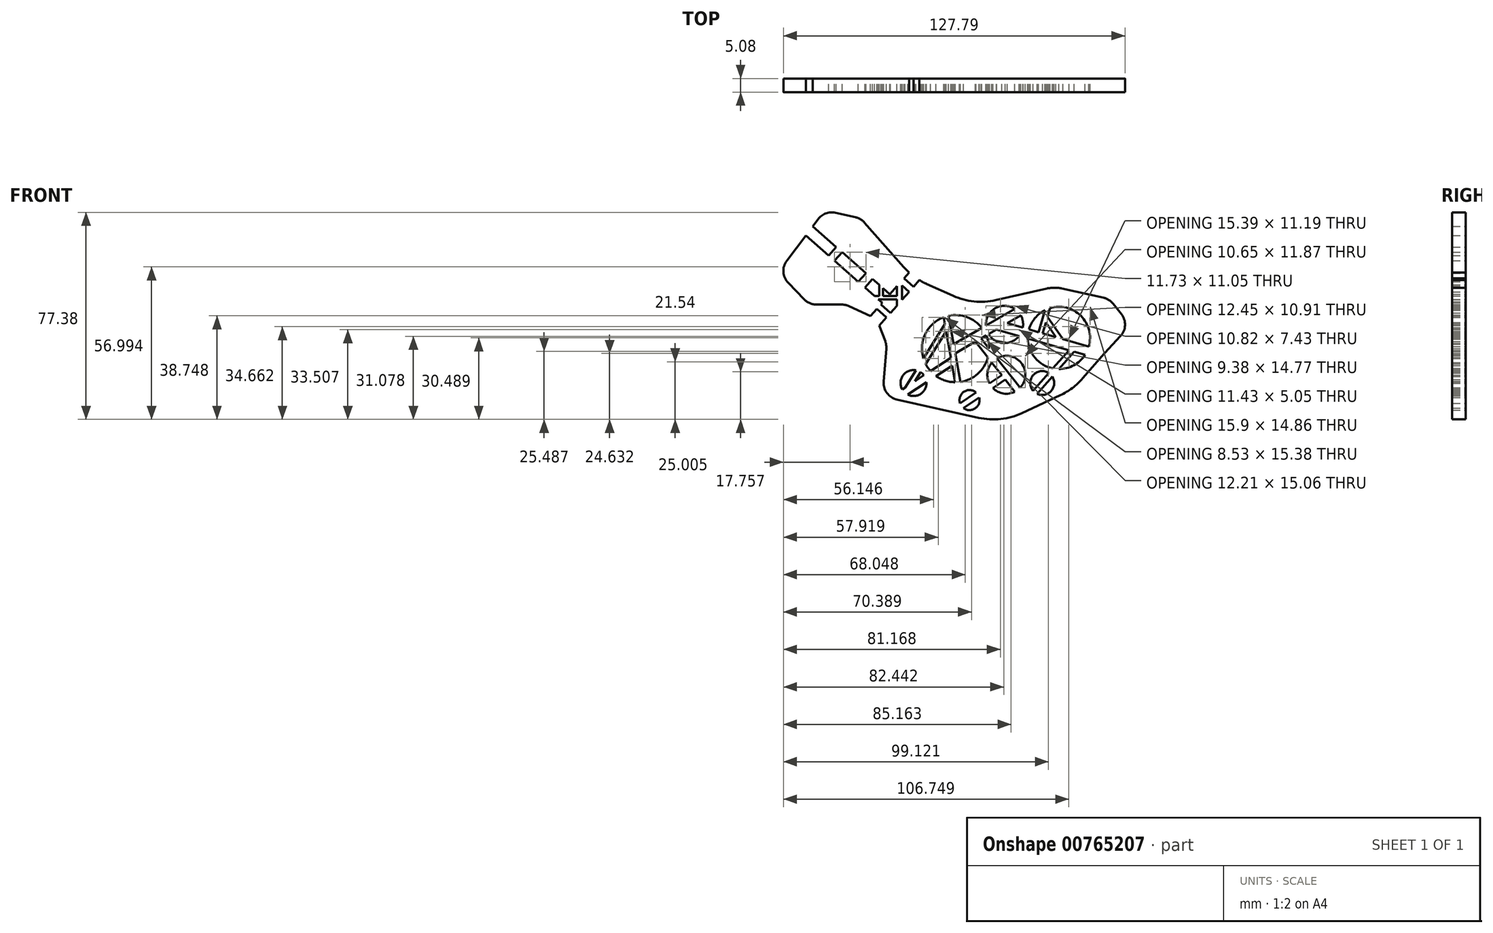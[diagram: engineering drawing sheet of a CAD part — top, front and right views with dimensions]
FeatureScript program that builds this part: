
annotation { "Feature Type Name" : "Feature", "Feature Type Description" : "" }
export const myFeature = defineFeature(function(context is Context, id is Id, definition is map)
    precondition{}
    {
        {
            var Q0;
            Q0=qCreatedBy(makeId("Front.planeOp"),FACE);
            var sketch = newSketch(context, id + "F0", { "sketchPlane" : qUnion([Q0])});
            skLineSegment(sketch, "E0", {"start": v(-47.4, 34.58) * mm, "end": v(-40.28, 44.05) * mm});
            skLineSegment(sketch, "E1", {"start": v(-29.25, 52.5) * mm, "end": v(-21.71, 50.83) * mm});
            skLineSegment(sketch, "E2", {"start": v(-18.34, 48.84) * mm, "end": v(-3.61, 32.2) * mm});
            skLineSegment(sketch, "E3", {"start": v(4.97, 25.88) * mm, "end": v(14.76, 21.48) * mm});
            skLineSegment(sketch, "E4", {"start": v(30.8, 19.86) * mm, "end": v(49.9, 24.2) * mm});
            skLineSegment(sketch, "E5", {"start": v(55.46, 24.2) * mm, "end": v(71.08, 20.73) * mm});
            skLineSegment(sketch, "E6", {"start": v(74.67, 18.5) * mm, "end": v(77.72, 14.67) * mm});
            skLineSegment(sketch, "E7", {"start": v(77.4, 6.37) * mm, "end": v(71.52, 0.08) * mm});
            skLineSegment(sketch, "E8", {"start": v(71.36, -0.09) * mm, "end": v(63.3, -9.36) * mm});
            skLineSegment(sketch, "E9", {"start": v(54.85, -15.72) * mm, "end": v(40.59, -22.36) * mm});
            skLineSegment(sketch, "E10", {"start": v(24.36, -24.13) * mm, "end": v(3.63, -19.52) * mm});
            skLineSegment(sketch, "E11", {"start": v(3.63, -19.52) * mm, "end": v(-6.19, -17.34) * mm});
            skLineSegment(sketch, "E12", {"start": v(-11.14, -10.65) * mm, "end": v(-10.18, 1.76) * mm});
            skLineSegment(sketch, "E13", {"start": v(-10.57, 4.47) * mm, "end": v(-12.77, 10.34) * mm});
            skLineSegment(sketch, "E14", {"start": v(-16.05, 13.88) * mm, "end": v(-24.15, 17.61) * mm});
            skLineSegment(sketch, "E15", {"start": v(-26.81, 18.2) * mm, "end": v(-36.27, 18.2) * mm});
            skLineSegment(sketch, "E16", {"start": v(-40.82, 20.11) * mm, "end": v(-46.88, 26.33) * mm});
            skPoint(sketch, "E17.visualSharp", {"position": v(-33.24, 53.4) * mm});
            skArc(sketch, "E17.filletArc", {"start": v(-29.25, 52.5) * mm, "mid": v(-32.82, 52.26) * mm, "end": v(-35.7, 50.13) * mm});
            skPoint(sketch, "E18.visualSharp", {"position": v(-19.7, 50.38) * mm});
            skArc(sketch, "E18.filletArc", {"start": v(-18.34, 48.84) * mm, "mid": v(-19.87, 50.1) * mm, "end": v(-21.71, 50.83) * mm});
            skPoint(sketch, "E19.visualSharp", {"position": v(0, 28.12) * mm});
            skArc(sketch, "E19.filletArc", {"start": v(-3.61, 32.2) * mm, "mid": v(-2.66, 31.19) * mm, "end": v(-1.65, 30.22) * mm});
            skPoint(sketch, "E20.visualSharp", {"position": v(22.5, 17.98) * mm});
            skArc(sketch, "E20.filletArc", {"start": v(14.76, 21.48) * mm, "mid": v(22.65, 19.36) * mm, "end": v(30.8, 19.86) * mm});
            skPoint(sketch, "E21.visualSharp", {"position": v(52.68, 24.82) * mm});
            skArc(sketch, "E21.filletArc", {"start": v(55.46, 24.2) * mm, "mid": v(52.68, 24.5) * mm, "end": v(49.9, 24.2) * mm});
            skPoint(sketch, "E22.visualSharp", {"position": v(73.27, 20.25) * mm});
            skArc(sketch, "E22.filletArc", {"start": v(74.67, 18.5) * mm, "mid": v(73.07, 19.92) * mm, "end": v(71.08, 20.73) * mm});
            skPoint(sketch, "E23.visualSharp", {"position": v(81.14, 10.38) * mm});
            skArc(sketch, "E23.filletArc", {"start": v(77.4, 6.37) * mm, "mid": v(79.1, 10.46) * mm, "end": v(77.72, 14.67) * mm});
            skPoint(sketch, "E24.visualSharp", {"position": v(71.44, 0) * mm});
            skArc(sketch, "E24.filletArc", {"start": v(71.52, 0.08) * mm, "mid": v(71.44, 0) * mm, "end": v(71.36, -0.09) * mm});
            skPoint(sketch, "E25.visualSharp", {"position": v(59.75, -13.44) * mm});
            skArc(sketch, "E25.filletArc", {"start": v(54.85, -15.72) * mm, "mid": v(59.41, -12.98) * mm, "end": v(63.3, -9.36) * mm});
            skPoint(sketch, "E26.visualSharp", {"position": v(32.77, -26) * mm});
            skArc(sketch, "E26.filletArc", {"start": v(24.36, -24.13) * mm, "mid": v(32.62, -24.58) * mm, "end": v(40.59, -22.36) * mm});
            skPoint(sketch, "E27.visualSharp", {"position": v(-11.57, -16.14) * mm});
            skArc(sketch, "E27.filletArc", {"start": v(-11.14, -10.65) * mm, "mid": v(-9.91, -14.92) * mm, "end": v(-6.19, -17.34) * mm});
            skPoint(sketch, "E28.visualSharp", {"position": v(-10.08, 3.16) * mm});
            skArc(sketch, "E28.filletArc", {"start": v(-10.18, 1.76) * mm, "mid": v(-10.23, 3.14) * mm, "end": v(-10.57, 4.47) * mm});
            skPoint(sketch, "E29.visualSharp", {"position": v(-13.69, 12.78) * mm});
            skPoint(sketch, "E30.visualSharp", {"position": v(-25.42, 18.2) * mm});
            skArc(sketch, "E30.filletArc", {"start": v(-24.15, 17.61) * mm, "mid": v(-25.45, 18.05) * mm, "end": v(-26.81, 18.2) * mm});
            skPoint(sketch, "E31.visualSharp", {"position": v(-38.95, 18.2) * mm});
            skArc(sketch, "E31.filletArc", {"start": v(-40.82, 20.11) * mm, "mid": v(-38.74, 18.7) * mm, "end": v(-36.27, 18.2) * mm});
            skPoint(sketch, "E32.visualSharp", {"position": v(-50.68, 30.23) * mm});
            skArc(sketch, "E32.filletArc", {"start": v(-47.4, 34.58) * mm, "mid": v(-48.67, 30.36) * mm, "end": v(-46.88, 26.33) * mm});
            skArc(sketch, "E33", {"start": v(42.75, 5.5) * mm, "mid": v(45.47, -1.75) * mm, "end": v(52.14, -5.7) * mm});
            skArc(sketch, "E34", {"start": v(25.6, 9.44) * mm, "mid": v(20.02, 13.5) * mm, "end": v(13.14, 14) * mm});
            skArc(sketch, "E35", {"start": v(29.28, -3.47) * mm, "mid": v(27.66, -7.25) * mm, "end": v(28.4, -11.3) * mm});
            skArc(sketch, "E36", {"start": v(28.05, 7.2) * mm, "mid": v(33.56, 3.82) * mm, "end": v(39.48, 6.43) * mm});
            skArc(sketch, "E37", {"start": v(3.88, -8.23) * mm, "mid": v(3.31, -7.6) * mm, "end": v(2.64, -7.07) * mm});
            skArc(sketch, "E38", {"start": v(18.66, -20.5) * mm, "mid": v(23.05, -20.63) * mm, "end": v(24.56, -16.5) * mm});
            skArc(sketch, "E39", {"start": v(50.62, -7.41) * mm, "mid": v(44.77, -8.17) * mm, "end": v(44.74, -14.07) * mm});
            skLineSegment(sketch, "E40", {"start": v(-16.05, 13.88) * mm, "end": v(-13.69, 16.56) * mm});
            skLineSegment(sketch, "E41", {"start": v(-12.77, 10.34) * mm, "end": v(-10.08, 13.39) * mm});
            skPoint(sketch, "E42.startSnap0", {"position": v(-5.28, 18.84) * mm});
            skLineSegment(sketch, "E43", {"start": v(-8.85, 22.05) * mm, "end": v(-11.42, 24.3) * mm});
            skArc(sketch, "E44.trimOffspring", {"start": v(2.21, 27.34) * mm, "mid": v(3.57, 26.57) * mm, "end": v(4.97, 25.88) * mm});
            skLineSegment(sketch, "E45.trimOffspring", {"start": v(-8.85, 22.05) * mm, "end": v(-6.2, 25.05) * mm});
            skLineSegment(sketch, "E46.trimOffspring", {"start": v(-37.7, 47.47) * mm, "end": v(-35.7, 50.13) * mm});
            skLineSegment(sketch, "E47", {"start": v(-31.75, 36.53) * mm, "end": v(-28.92, 39.74) * mm});
            skLineSegment(sketch, "E48", {"start": v(-29.54, 34.58) * mm, "end": v(-26.71, 37.8) * mm});
            skLineSegment(sketch, "E49", {"start": v(-20.64, 26.74) * mm, "end": v(-17.81, 29.95) * mm});
            skLineSegment(sketch, "E50", {"start": v(-18.16, 24.55) * mm, "end": v(-15.33, 27.76) * mm});
            skLineSegment(sketch, "E51.trimOffspring", {"start": v(-31.75, 36.53) * mm, "end": v(-40.28, 44.05) * mm});
            skLineSegment(sketch, "E52.trimOffspring", {"start": v(-28.92, 39.74) * mm, "end": v(-37.7, 47.47) * mm});
            skLineSegment(sketch, "E53.trimOffspring", {"start": v(-17.81, 29.95) * mm, "end": v(-26.71, 37.8) * mm});
            skLineSegment(sketch, "E54.trimOffspring", {"start": v(-20.64, 26.74) * mm, "end": v(-29.54, 34.58) * mm});
            skLineSegment(sketch, "E55", {"start": v(-4.29, 25.28) * mm, "end": v(-1.65, 22.96) * mm});
            skLineSegment(sketch, "E56", {"start": v(-13.69, 16.56) * mm, "end": v(-10.08, 13.39) * mm});
            skLineSegment(sketch, "E57", {"start": v(-8.57, 15.1) * mm, "end": v(-12.17, 18.28) * mm});
            skLineSegment(sketch, "E58", {"start": v(0, 24.83) * mm, "end": v(-3.6, 28) * mm});
            skLineSegment(sketch, "E59.trimOffspring", {"start": v(-3.6, 28) * mm, "end": v(-1.65, 30.22) * mm});
            skLineSegment(sketch, "E60.trimOffspring", {"start": v(0, 24.83) * mm, "end": v(2.21, 27.34) * mm});
            skLineSegment(sketch, "E61.trimOffspring", {"start": v(-8.57, 15.1) * mm, "end": v(-6.2, 17.78) * mm});
            skLineSegment(sketch, "E62.trimOffspring", {"start": v(-12.17, 18.28) * mm, "end": v(-11.68, 18.84) * mm});
            skLineSegment(sketch, "E63", {"start": v(-4.29, 25.28) * mm, "end": v(-4.29, 19.96) * mm});
            skLineSegment(sketch, "E64", {"start": v(-6.2, 21.42) * mm, "end": v(-11.42, 21.42) * mm});
            skLineSegment(sketch, "E65", {"start": v(-6.2, 20.13) * mm, "end": v(-13.14, 20.13) * mm});
            skPoint(sketch, "E66.orphan", {"position": v(-5.25, 26.13) * mm});
            skLineSegment(sketch, "E67.trimOffspring", {"start": v(-4.29, 19.96) * mm, "end": v(-1.65, 22.96) * mm});
            skLineSegment(sketch, "E68.trimOffspring", {"start": v(-6.2, 20.13) * mm, "end": v(-6.2, 17.78) * mm});
            skLineSegment(sketch, "E69.trimOffspring", {"start": v(-14.6, 21.42) * mm, "end": v(-18.16, 24.55) * mm});
            skLineSegment(sketch, "E70", {"start": v(-13.14, 20.13) * mm, "end": v(-11.68, 18.84) * mm});
            skLineSegment(sketch, "E71", {"start": v(-6.2, 21.42) * mm, "end": v(-6.2, 25.05) * mm});
            skLineSegment(sketch, "E72", {"start": v(-12.84, 21.42) * mm, "end": v(-12.84, 25.56) * mm});
            skLineSegment(sketch, "E73", {"start": v(-11.42, 21.42) * mm, "end": v(-11.42, 24.3) * mm});
            skLineSegment(sketch, "E74.trimOffspring", {"start": v(-12.84, 25.56) * mm, "end": v(-15.33, 27.76) * mm});
            skLineSegment(sketch, "E75.trimOffspring", {"start": v(-12.84, 21.42) * mm, "end": v(-14.6, 21.42) * mm});
            skLineSegment(sketch, "E76", {"start": v(11.27, 13.45) * mm, "end": v(11.73, 10.84) * mm});
            skLineSegment(sketch, "E77", {"start": v(13.14, 14) * mm, "end": v(15.02, 3.32) * mm});
            skLineSegment(sketch, "E78", {"start": v(15.02, 3.32) * mm, "end": v(25.6, 9.44) * mm});
            skLineSegment(sketch, "E79", {"start": v(15.6, 0) * mm, "end": v(23.1, 4.34) * mm});
            skLineSegment(sketch, "E80.trimOffspring", {"start": v(28.05, 7.2) * mm, "end": v(30.94, 8.88) * mm});
            skLineSegment(sketch, "E81.trimOffspring", {"start": v(27.08, 10.3) * mm, "end": v(37.9, 16.56) * mm});
            skArc(sketch, "E82.trimOffspring", {"start": v(37.9, 16.56) * mm, "mid": v(30.54, 16.8) * mm, "end": v(27.08, 10.3) * mm});
            skLineSegment(sketch, "E83.trimOffspring", {"start": v(15.6, 0) * mm, "end": v(17.49, -10.72) * mm});
            skArc(sketch, "E84.trimOffspring", {"start": v(11.27, 13.45) * mm, "mid": v(4.45, 7.25) * mm, "end": v(3.7, -1.93) * mm});
            skArc(sketch, "E85.trimOffspring", {"start": v(17.49, -10.72) * mm, "mid": v(24.01, -7.7) * mm, "end": v(27.82, -1.62) * mm});
            skLineSegment(sketch, "E86", {"start": v(14.44, -4.58) * mm, "end": v(8.42, -8.51) * mm});
            skLineSegment(sketch, "E87.trimOffspring", {"start": v(14.44, -4.58) * mm, "end": v(15.55, -10.84) * mm});
            skArc(sketch, "E88.trimOffspring", {"start": v(8.42, -8.51) * mm, "mid": v(11.8, -10.22) * mm, "end": v(15.55, -10.84) * mm});
            skArc(sketch, "E89.trimOffspring", {"start": v(-2.2, -15.47) * mm, "mid": v(2.66, -15.2) * mm, "end": v(4.85, -10.85) * mm});
            skLineSegment(sketch, "E90", {"start": v(23.1, 4.34) * mm, "end": v(27.82, -1.62) * mm});
            skLineSegment(sketch, "E91", {"start": v(25.24, 5.58) * mm, "end": v(39.88, -12.9) * mm});
            skLineSegment(sketch, "E92.trimOffspring", {"start": v(25.24, 5.58) * mm, "end": v(27.22, 6.72) * mm});
            skArc(sketch, "E93.trimOffspring", {"start": v(28.26, 1.76) * mm, "mid": v(28, 4.3) * mm, "end": v(27.22, 6.72) * mm});
            skArc(sketch, "E94.trimOffspring", {"start": v(39.88, -12.9) * mm, "mid": v(40.28, -3.63) * mm, "end": v(31.16, -1.9) * mm});
            skLineSegment(sketch, "E95", {"start": v(34.36, -9.88) * mm, "end": v(29.68, -13.04) * mm});
            skLineSegment(sketch, "E96", {"start": v(33.01, -8.18) * mm, "end": v(28.4, -11.3) * mm});
            skArc(sketch, "E97.trimOffspring", {"start": v(23.4, -14.68) * mm, "mid": v(18.84, -14.4) * mm, "end": v(17.4, -18.75) * mm});
            skLineSegment(sketch, "E98.trimOffspring", {"start": v(24.56, -16.5) * mm, "end": v(18.66, -20.5) * mm});
            skLineSegment(sketch, "E99.trimOffspring", {"start": v(23.4, -14.68) * mm, "end": v(17.4, -18.75) * mm});
            skArc(sketch, "E100.trimOffspring", {"start": v(29.68, -13.04) * mm, "mid": v(33.58, -15.04) * mm, "end": v(37.92, -14.37) * mm});
            skLineSegment(sketch, "E101.trimOffspring", {"start": v(34.36, -9.88) * mm, "end": v(37.92, -14.37) * mm});
            skLineSegment(sketch, "E102", {"start": v(11.73, 10.84) * mm, "end": v(3.7, -1.93) * mm});
            skLineSegment(sketch, "E103", {"start": v(12.2, 8.14) * mm, "end": v(4.55, -4.03) * mm});
            skLineSegment(sketch, "E104.trimOffspring", {"start": v(12.2, 8.14) * mm, "end": v(13.93, -1.65) * mm});
            skArc(sketch, "E105.trimOffspring", {"start": v(4.55, -4.03) * mm, "mid": v(5.36, -5.39) * mm, "end": v(6.33, -6.63) * mm});
            skArc(sketch, "E106.trimOffspring", {"start": v(0.9, -6.37) * mm, "mid": v(-3.94, -8.31) * mm, "end": v(-4.23, -13.53) * mm});
            skLineSegment(sketch, "E107.trimOffspring", {"start": v(-3.16, -12.83) * mm, "end": v(-4.23, -13.53) * mm});
            skLineSegment(sketch, "E108", {"start": v(30.94, 8.88) * mm, "end": v(58.14, 1.1) * mm});
            skLineSegment(sketch, "E109", {"start": v(65.57, 2.5) * mm, "end": v(55.86, 5.28) * mm});
            skLineSegment(sketch, "E110.trimOffspring", {"start": v(35.03, 11.24) * mm, "end": v(40.1, 14.18) * mm});
            skArc(sketch, "E111.trimOffspring", {"start": v(40.89, 9.56) * mm, "mid": v(40.9, 11.94) * mm, "end": v(40.1, 14.18) * mm});
            skArc(sketch, "E112.trimOffspring", {"start": v(65.57, 2.5) * mm, "mid": v(62.56, 14) * mm, "end": v(51.03, 16.87) * mm});
            skLineSegment(sketch, "E113", {"start": v(46.79, 7.88) * mm, "end": v(49.15, 16.12) * mm});
            skLineSegment(sketch, "E114", {"start": v(48.33, 7.44) * mm, "end": v(49.5, 11.51) * mm});
            skLineSegment(sketch, "E115", {"start": v(49.5, 11.51) * mm, "end": v(53.25, 6.03) * mm});
            skLineSegment(sketch, "E116", {"start": v(50.12, 13.68) * mm, "end": v(55.86, 5.28) * mm});
            skLineSegment(sketch, "E117.trimOffspring", {"start": v(46.79, 7.88) * mm, "end": v(35.03, 11.24) * mm});
            skArc(sketch, "E118.trimOffspring", {"start": v(49.15, 16.12) * mm, "mid": v(45.41, 13.14) * mm, "end": v(43.19, 8.9) * mm});
            skLineSegment(sketch, "E119.trimOffspring", {"start": v(50.12, 13.68) * mm, "end": v(51.03, 16.87) * mm});
            skLineSegment(sketch, "E120.trimOffspring", {"start": v(53.25, 6.03) * mm, "end": v(48.33, 7.44) * mm});
            skLineSegment(sketch, "E121", {"start": v(60.11, 0.53) * mm, "end": v(54.42, -5.91) * mm});
            skLineSegment(sketch, "E122", {"start": v(58.14, 1.1) * mm, "end": v(52.14, -5.7) * mm});
            skLineSegment(sketch, "E123.trimOffspring", {"start": v(60.11, 0.53) * mm, "end": v(64.14, -0.62) * mm});
            skArc(sketch, "E124.trimOffspring", {"start": v(54.42, -5.91) * mm, "mid": v(59.95, -4.5) * mm, "end": v(64.14, -0.62) * mm});
            skArc(sketch, "E125.trimOffspring", {"start": v(46.22, -15.2) * mm, "mid": v(51.49, -14.1) * mm, "end": v(51.92, -8.75) * mm});
            skLineSegment(sketch, "E126.trimOffspring", {"start": v(50.62, -7.41) * mm, "end": v(44.74, -14.07) * mm});
            skLineSegment(sketch, "E127.trimOffspring", {"start": v(51.92, -8.75) * mm, "end": v(46.22, -15.2) * mm});
            skLineSegment(sketch, "E128.trimOffspring", {"start": v(4.85, -10.85) * mm, "end": v(-2.2, -15.47) * mm});
            skLineSegment(sketch, "E129.trimOffspring", {"start": v(3.88, -8.23) * mm, "end": v(0.54, -10.41) * mm});
            skLineSegment(sketch, "E130.trimOffspring", {"start": v(2.64, -7.07) * mm, "end": v(0.54, -10.41) * mm});
            skLineSegment(sketch, "E131.trimOffspring", {"start": v(0.9, -6.37) * mm, "end": v(-3.16, -12.83) * mm});
            skLineSegment(sketch, "E132", {"start": v(13.93, -1.65) * mm, "end": v(6.33, -6.63) * mm});
            skLineSegment(sketch, "E133.trimOffspring", {"start": v(29.28, -3.47) * mm, "end": v(33.01, -8.18) * mm});
            skSolve(sketch);
        }
        {
            var Q0;
            Q0=makeQuery(id+"F0.imprint","IMPRINT",FACE,{"disambiguationData":[TD([[makeQuery(id+"F0.imprint","IMPRINT",EDGE,{"derivedFrom":sQuery(id+"F0.wireOp",EDGE,"E0")}),-1.0]])]});
            extrude(context, id + "F1", {"entities" : qUnion([Q0]), "depth" : 5.08 * mm, "offsetDistance" : 25.4 * mm});
        }
    });
